# Revit family: Faucet-Lavatory-Grohe-Bauloop-20225000
name_source: partatom
category: Plumbing Fixtures
revit_build: Autodesk Revit 2018 (Build: 20170223_1515(x64)
units: mm (PartAtom-declared; Revit-internal decimal feet)

## family parameters
Always vertical = No
Cut with Voids When Loaded = No
OmniClass Number = 23.45.55.17
OmniClass Title = Mixing Faucets
Part Type = Normal
Room Calculation Point = No
Round Connector Dimension = Use Diameter
Shared = Yes
Work Plane-Based = Yes

## types (1)
- 20225000
    CW Connection = Yes
    CWFU = 1.5
    Cold Water Connection Diameter = 3/8"
    Default Elevation = 0"
    Description = 8" Widespread 2-Handle S-Size Bathroom Faucet 1.2 GPM
    Finish = Metal-Grohe-000-StarLight Chrome
    Flow Rate = 1.2 GPM
    HW Connection = Yes
    HWFU = 1.5
    Handle Width Constraint = 8"
    Height = 5"
    Hot Water Connection Diameter = 0"
    Installation Type = Deck Mounted
    Manufacturer = Grohe
    Model = 20225000
    Price = Prices may vary. Please consult Manufacturer Representative for most up-to-date price list.
    Product Documentation Link = https://americanstandard.box.com
    Product Page URL = https://www.grohe.us
    Revised Date = 04/16/2021
    URL = https://www.grohe.us
    Vent Connection = No
    WFU = 2
    Warranty Information = Limited Lifetime Warranty
    Waste Connection = No
    Width = 8"

## geometry (parser evidence)
native form markers: Sweep x2
no freeform markers — native parametric forms only
